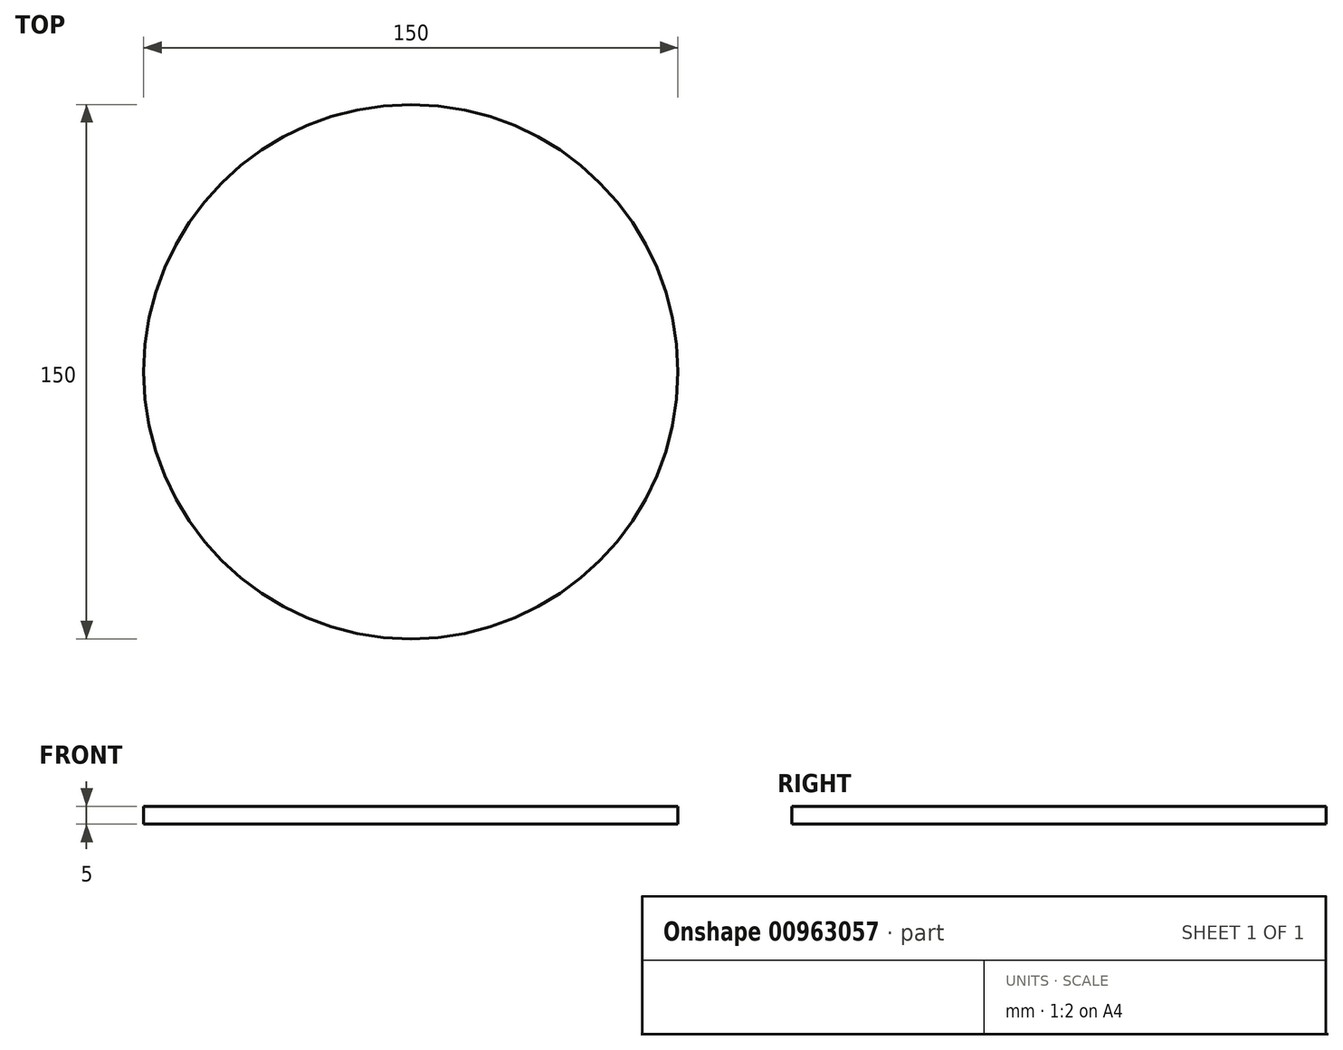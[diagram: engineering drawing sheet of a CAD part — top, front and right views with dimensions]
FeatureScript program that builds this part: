
annotation { "Feature Type Name" : "Feature", "Feature Type Description" : "" }
export const myFeature = defineFeature(function(context is Context, id is Id, definition is map)
    precondition{}
    {
        {
            var Q0;
            Q0=qCreatedBy(makeId("Top.planeOp"),FACE);
            var sketch = newSketch(context, id + "F0", { "sketchPlane" : qUnion([Q0])});
            skCircle(sketch, "E0", {"center": v(0, 0) * mm, "radius": 75 * mm});
            skSolve(sketch);
        }
        {
            var Q0;
            Q0 = qSketchRegion(id + "F0", true);
            extrude(context, id + "F1", {"entities" : qUnion([Q0]), "depth" : 5 * mm, "offsetDistance" : 25 * mm});
        }
    });
